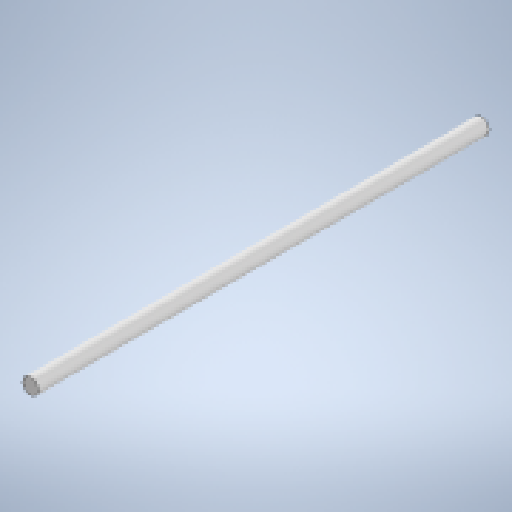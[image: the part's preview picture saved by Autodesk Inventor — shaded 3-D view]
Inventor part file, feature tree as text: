
AUTODESK INVENTOR PART (.ipt)
format: ipt  version: 2025.3 (Build 293356030, 356C)  size: 134,144 bytes
history: native  units: mm
features: extrude x1, sketch x1
ambient origin geometry x8: Origin, YZ Plane, XZ Plane, XY Plane, X Axis, Y Axis, Z Axis, Center Point
bodies: Solid1 (feature_tree)
feature tree (2):
  extrude  "Extrusion1"  Depth=30.0mm TaperAngle=0.0deg
  sketch  "Sketch1"  dims[d0=1.75mm d1=30.0mm d2=0.0mm]
